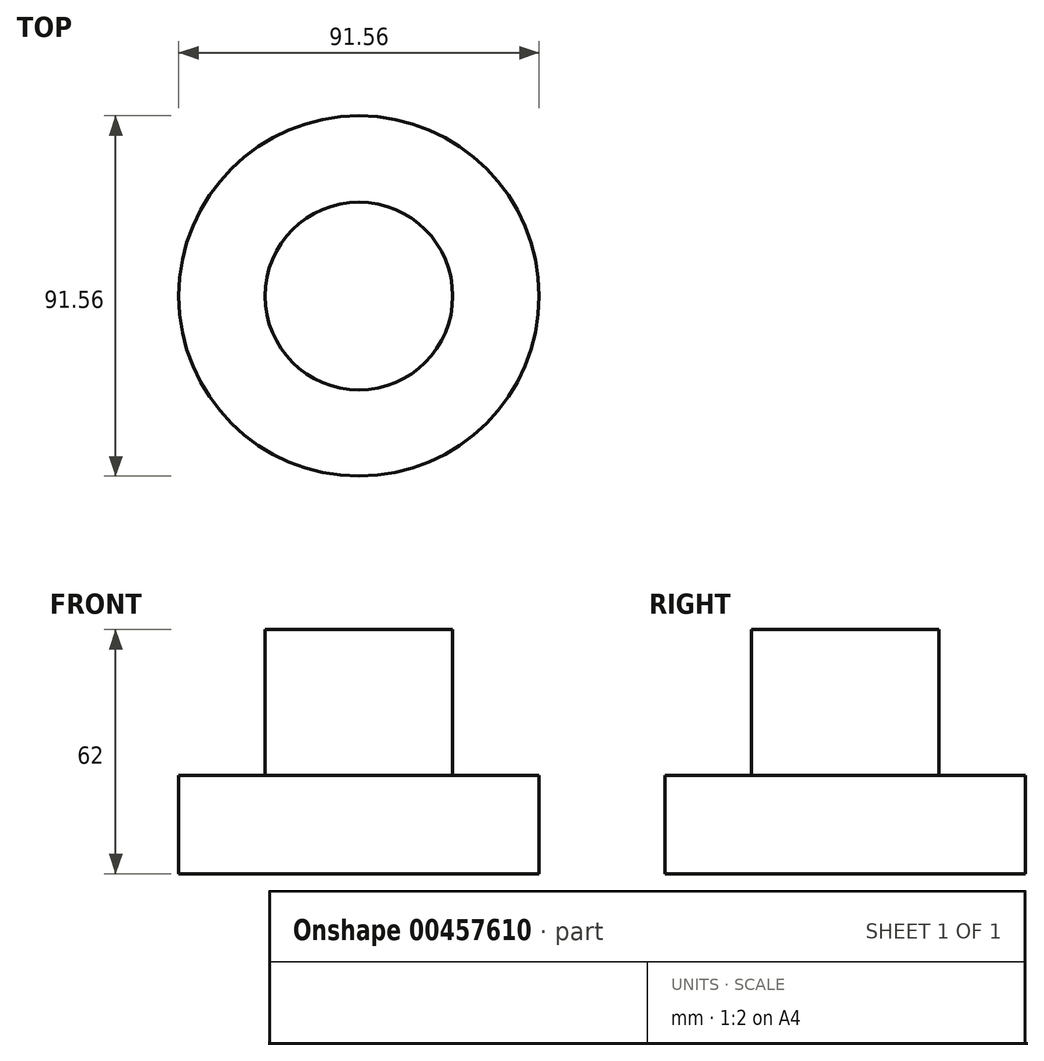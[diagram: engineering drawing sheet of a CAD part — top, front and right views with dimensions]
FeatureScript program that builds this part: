
annotation { "Feature Type Name" : "Feature", "Feature Type Description" : "" }
export const myFeature = defineFeature(function(context is Context, id is Id, definition is map)
    precondition{}
    {
        {
            var Q0;
            Q0=qCreatedBy(makeId("Top.planeOp"),FACE);
            var sketch = newSketch(context, id + "F0", { "sketchPlane" : qUnion([Q0])});
            skCircle(sketch, "E0", {"center": v(0, 0) * mm, "radius": 23.84 * mm});
            skSolve(sketch);
        }
        {
            var Q0;
            Q0=qCreatedBy(makeId("Top.planeOp"),FACE);
            var sketch = newSketch(context, id + "F1", { "sketchPlane" : qUnion([Q0])});
            skCircle(sketch, "E1", {"center": v(0, 0) * mm, "radius": 21.42 * mm});
            skSolve(sketch);
        }
        {
            var Q0;
            Q0=makeQuery(id+"F0.imprint","IMPRINT",FACE,{"disambiguationData":[TD([[makeQuery(id+"F0.imprint","IMPRINT",EDGE,{"derivedFrom":sQuery(id+"F0.wireOp",EDGE,"E0")}),1.0]])]});
            extrude(context, id + "F2", {"entities" : qUnion([Q0]), "depth" : 62 * mm});
        }
        {
            var Q0;
            Q0=makeQuery(id+"F1.imprint","IMPRINT",FACE,{"disambiguationData":[TD([[makeQuery(id+"F1.imprint","IMPRINT",EDGE,{"derivedFrom":sQuery(id+"F1.wireOp",EDGE,"E1")}),1.0]])]});
            var sketch = newSketch(context, id + "F3", { "sketchPlane" : qUnion([Q0])});
            skCircle(sketch, "E2", {"center": v(0, 0) * mm, "radius": 45.78 * mm});
            skSolve(sketch);
        }
        {
            var Q0;
            Q0=makeQuery(id+"F3.imprint","IMPRINT",FACE,{"disambiguationData":[TD([[makeQuery(id+"F3.imprint","IMPRINT",EDGE,{"derivedFrom":sQuery(id+"F3.wireOp",EDGE,"E2")}),1.0]])]});
            extrude(context, id + "F4", {"entities" : qUnion([Q0]), "operationType" : NewBodyOperationType.ADD, "depth" : 25 * mm});
        }
    });
